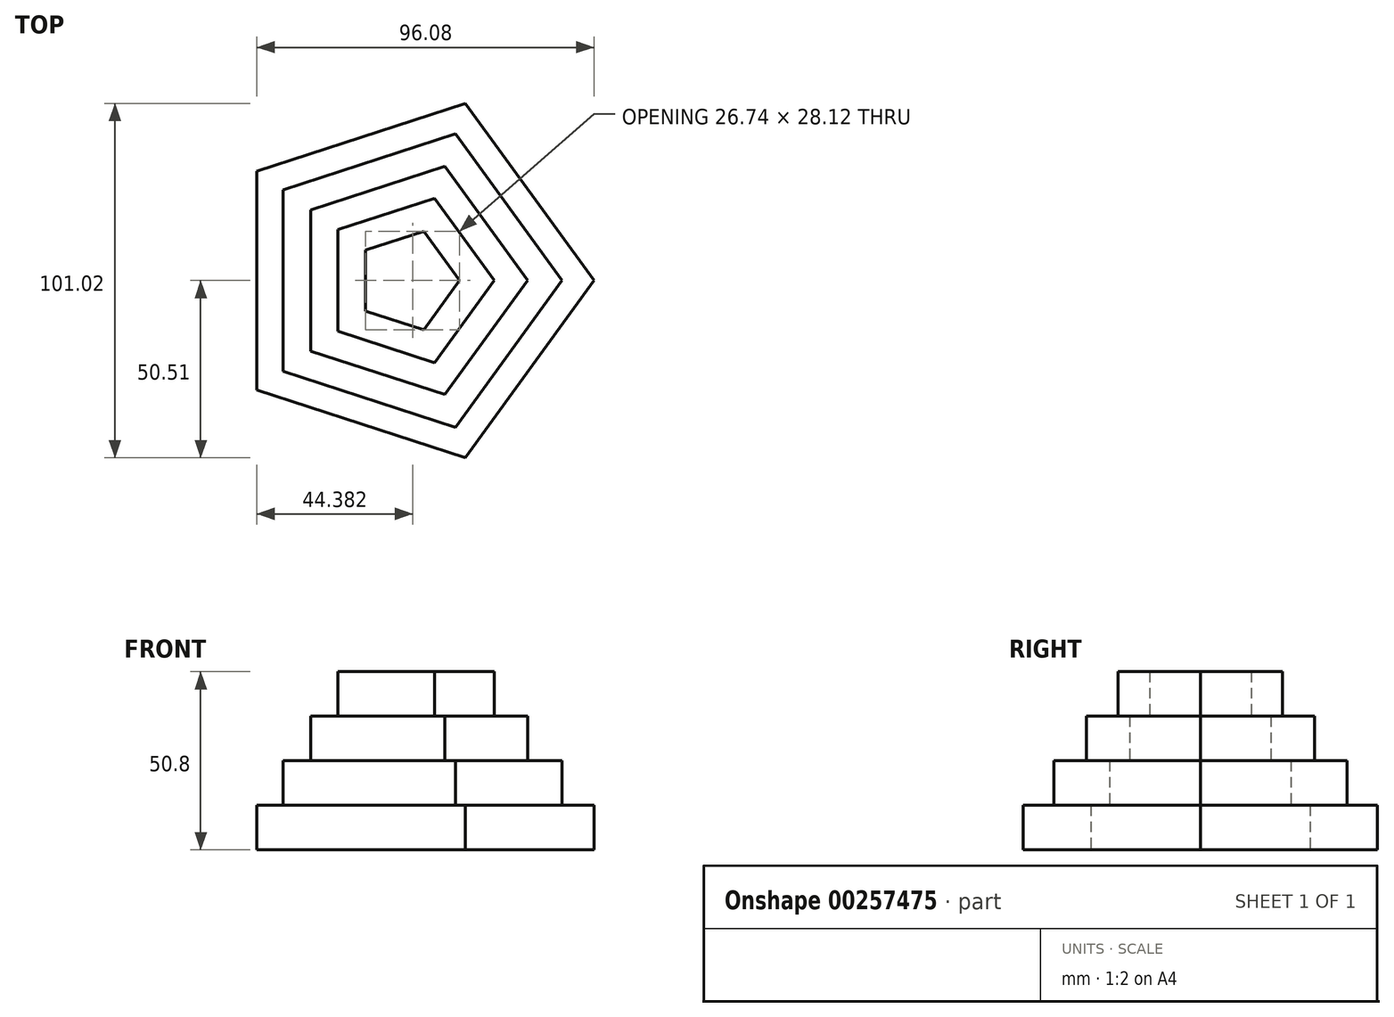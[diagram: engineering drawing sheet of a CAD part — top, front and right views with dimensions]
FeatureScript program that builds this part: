
annotation { "Feature Type Name" : "Feature", "Feature Type Description" : "" }
export const myFeature = defineFeature(function(context is Context, id is Id, definition is map)
    precondition{}
    {
        {
            var Q0;
            Q0=qCreatedBy(makeId("Top.planeOp"),FACE);
            var sketch = newSketch(context, id + "F0", { "sketchPlane" : qUnion([Q0])});
            skCircle(sketch, "E0.cCircle", {"center": v(0, 0) * mm, "radius": 42.97 * mm, "construction": true});
            skLineSegment(sketch, "E0.0", {"start": v(-42.97, -31.22) * mm, "end": v(-42.97, 31.22) * mm});
            skLineSegment(sketch, "E0.1", {"start": v(-42.97, 31.22) * mm, "end": v(16.41, 50.51) * mm});
            skLineSegment(sketch, "E0.2", {"start": v(16.41, 50.51) * mm, "end": v(53.11, 0) * mm});
            skLineSegment(sketch, "E0.3", {"start": v(53.11, 0) * mm, "end": v(16.41, -50.51) * mm});
            skLineSegment(sketch, "E0.4", {"start": v(16.41, -50.51) * mm, "end": v(-42.97, -31.22) * mm});
            skPoint(sketch, "E0.0.midPoint", {"position": v(-42.97, 0) * mm});
            skCircle(sketch, "E1.cCircle", {"center": v(0, 0) * mm, "radius": 35.56 * mm, "construction": true});
            skLineSegment(sketch, "E1.0", {"start": v(-35.56, -25.84) * mm, "end": v(-35.56, 25.84) * mm});
            skLineSegment(sketch, "E1.1", {"start": v(-35.56, 25.84) * mm, "end": v(13.58, 41.8) * mm});
            skLineSegment(sketch, "E1.2", {"start": v(13.58, 41.8) * mm, "end": v(43.95, 0) * mm});
            skLineSegment(sketch, "E1.3", {"start": v(43.95, 0) * mm, "end": v(13.58, -41.8) * mm});
            skLineSegment(sketch, "E1.4", {"start": v(13.58, -41.8) * mm, "end": v(-35.56, -25.84) * mm});
            skPoint(sketch, "E1.0.midPoint", {"position": v(-35.56, 0) * mm});
            skCircle(sketch, "E2.cCircle", {"center": v(0, 0) * mm, "radius": 27.67 * mm, "construction": true});
            skLineSegment(sketch, "E2.0", {"start": v(34.2, 0) * mm, "end": v(10.57, -32.53) * mm});
            skLineSegment(sketch, "E2.1", {"start": v(10.57, -32.53) * mm, "end": v(-27.67, -20.1) * mm});
            skLineSegment(sketch, "E2.2", {"start": v(-27.67, -20.1) * mm, "end": v(-27.67, 20.1) * mm});
            skLineSegment(sketch, "E2.3", {"start": v(-27.67, 20.1) * mm, "end": v(10.57, 32.53) * mm});
            skLineSegment(sketch, "E2.4", {"start": v(10.57, 32.53) * mm, "end": v(34.2, 0) * mm});
            skPoint(sketch, "E2.0.midPoint", {"position": v(22.38, -16.26) * mm});
            skCircle(sketch, "E3.cCircle", {"center": v(0, 0) * mm, "radius": 19.94 * mm, "construction": true});
            skLineSegment(sketch, "E3.0", {"start": v(24.64, 0) * mm, "end": v(7.61, -23.44) * mm});
            skLineSegment(sketch, "E3.1", {"start": v(7.61, -23.44) * mm, "end": v(-19.94, -14.48) * mm});
            skLineSegment(sketch, "E3.2", {"start": v(-19.94, -14.48) * mm, "end": v(-19.94, 14.48) * mm});
            skLineSegment(sketch, "E3.3", {"start": v(-19.94, 14.48) * mm, "end": v(7.61, 23.44) * mm});
            skLineSegment(sketch, "E3.4", {"start": v(7.61, 23.44) * mm, "end": v(24.64, 0) * mm});
            skPoint(sketch, "E3.0.midPoint", {"position": v(16.13, -11.72) * mm});
            skCircle(sketch, "E4.cCircle", {"center": v(0, 0) * mm, "radius": 11.96 * mm, "construction": true});
            skLineSegment(sketch, "E4.0", {"start": v(14.78, 0) * mm, "end": v(4.57, -14.06) * mm});
            skLineSegment(sketch, "E4.1", {"start": v(4.57, -14.06) * mm, "end": v(-11.96, -8.69) * mm});
            skLineSegment(sketch, "E4.2", {"start": v(-11.96, -8.69) * mm, "end": v(-11.96, 8.69) * mm});
            skLineSegment(sketch, "E4.3", {"start": v(-11.96, 8.69) * mm, "end": v(4.57, 14.06) * mm});
            skLineSegment(sketch, "E4.4", {"start": v(4.57, 14.06) * mm, "end": v(14.78, 0) * mm});
            skPoint(sketch, "E4.0.midPoint", {"position": v(9.68, -7.03) * mm});
            skSolve(sketch);
        }
        {
            var Q0;
            Q0=makeQuery(id+"F0.imprint","IMPRINT",FACE,{"disambiguationData":[TD([[makeQuery(id+"F0.imprint","IMPRINT",EDGE,{"derivedFrom":sQuery(id+"F0.wireOp",EDGE,"E0.0")}),-1.0]])]});
            extrude(context, id + "F1", {"entities" : qUnion([Q0]), "depth" : 12.7 * mm});
        }
        {
            var Q0;
            Q0=makeQuery(id+"F0.imprint","IMPRINT",FACE,{"disambiguationData":[TD([[makeQuery(id+"F0.imprint","IMPRINT",EDGE,{"derivedFrom":sQuery(id+"F0.wireOp",EDGE,"E1.0")}),-1.0]])]});
            extrude(context, id + "F2", {"entities" : qUnion([Q0]), "operationType" : NewBodyOperationType.ADD, "depth" : 25.4 * mm});
        }
        {
            var Q0;
            Q0=makeQuery(id+"F0.imprint","IMPRINT",FACE,{"disambiguationData":[TD([[makeQuery(id+"F0.imprint","IMPRINT",EDGE,{"derivedFrom":sQuery(id+"F0.wireOp",EDGE,"E2.0")}),-1.0]])]});
            extrude(context, id + "F3", {"entities" : qUnion([Q0]), "operationType" : NewBodyOperationType.ADD, "depth" : 38.1 * mm});
        }
        {
            var Q0;
            Q0=makeQuery(id+"F0.imprint","IMPRINT",FACE,{"disambiguationData":[TD([[makeQuery(id+"F0.imprint","IMPRINT",EDGE,{"derivedFrom":sQuery(id+"F0.wireOp",EDGE,"E3.0")}),-1.0]])]});
            extrude(context, id + "F4", {"entities" : qUnion([Q0]), "operationType" : NewBodyOperationType.ADD, "depth" : 50.8 * mm});
        }
    });
